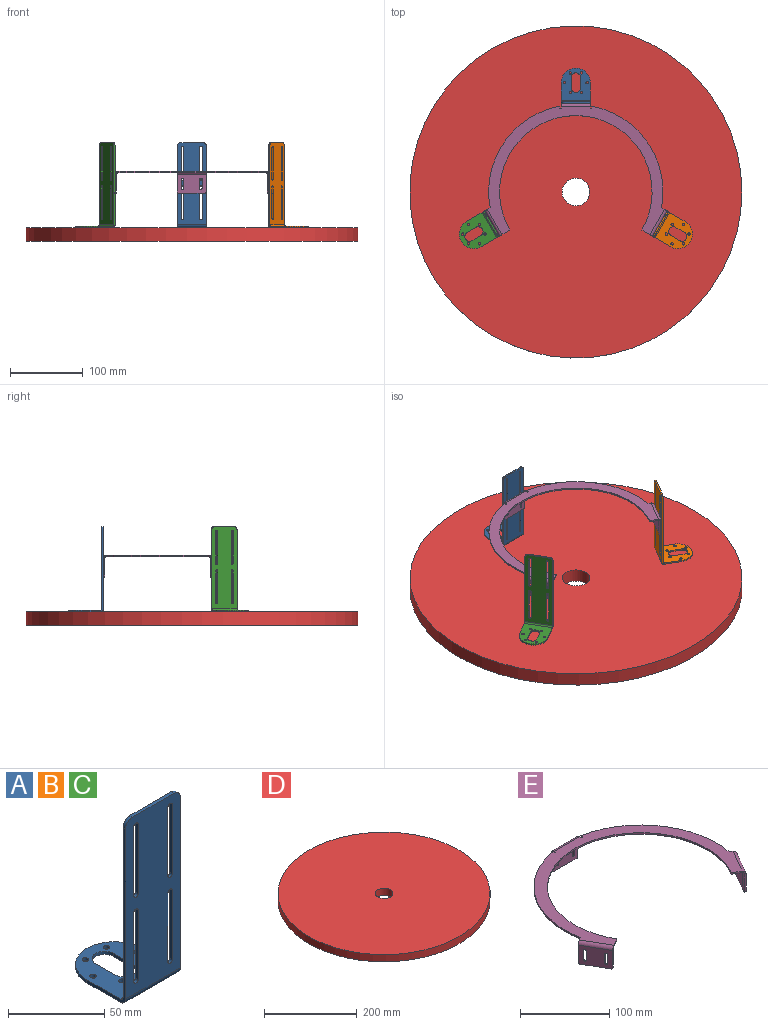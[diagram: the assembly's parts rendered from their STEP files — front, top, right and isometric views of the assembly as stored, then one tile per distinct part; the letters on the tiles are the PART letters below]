
ASSEMBLY  parts=5 mates=6
PART A: 38 faces, bbox 40x48.5x117 mm
  f0: plane 113x40mm, normal (0,1,0), area 3916.5mm2, adj f1,f3,f4,f5,f6,f7,f8,f9
  f1: cylinder r=1.6mm len=3.2mm, axis (0,-1,0), area 10.1mm2, adj f0,f2,f36,f37
  f2: plane 113x40mm, normal (0,-1,0), area 3916.5mm2, adj f1,f3,f4,f5,f6,f7,f8,f9
  f3: plane 43.8x2mm, normal (-1,0,0), area 87.6mm2, adj f0,f2,f5,f6
  f4: plane 43.8x2mm, normal (1,0,0), area 87.6mm2, adj f0,f2,f5,f6
  f5: cylinder r=1.6mm len=3.2mm, axis (0,-1,0), area 10.1mm2, adj f0,f2,f3,f4
  f6: cylinder r=1.6mm len=3.2mm, axis (0,-1,0), area 10.1mm2, adj f0,f2,f3,f4
  f7: cylinder r=1.6mm len=3.2mm, axis (0,-1,0), area 10.1mm2, adj f0,f2,f36,f37
  f8: cylinder r=1.6mm len=3.2mm, axis (0,-1,0), area 10.1mm2, adj f0,f2,f32,f34
  f9: cylinder r=1.6mm len=3.2mm, axis (0,-1,0), area 10.1mm2, adj f0,f2,f32,f34
  f10: cylinder r=1.6mm len=3.2mm, axis (0,-1,0), area 10.1mm2, adj f0,f2,f31,f35
  f11: cylinder r=5mm len=5mm, axis (0,1,0), area 15.7mm2, adj f0,f2,f14,f33
  f12: cylinder r=5mm len=5mm, axis (0,-1,0), area 15.7mm2, adj f0,f2,f15,f33
  f13: cylinder r=1.6mm len=3.2mm, axis (0,-1,0), area 10.1mm2, adj f0,f2,f31,f35
  f14: plane 112x28.5mm, normal (1,0,0), area 274.4mm2, adj f0,f2,f11,f16,f17,f18,f29,f30
  f15: plane 112x28.5mm, normal (-1,0,0), area 274.4mm2, adj f0,f2,f12,f16,f17,f18,f29,f30
  f16: cylinder r=20mm len=40mm, axis (0,0,-1), area 125.7mm2, adj f14,f15,f17,f18
  f17: plane 44.5x40mm, normal (0,0,-1), area 1242.3mm2, adj f14,f15,f16,f19,f20,f21,f22,f23
  f18: plane 44.5x40mm, normal (0,0,1), area 1242.3mm2, adj f14,f15,f16,f19,f20,f21,f22,f23
  f19: cylinder r=1.65mm len=3.3mm, axis (0,0,1), area 20.7mm2, adj f17,f18
  f20: cylinder r=1.65mm len=3.3mm, axis (0,0,1), area 20.7mm2, adj f17,f18
  f21: cylinder r=1.65mm len=3.3mm, axis (0,0,1), area 20.7mm2, adj f17,f18
  f22: cylinder r=1.65mm len=3.3mm, axis (0,0,1), area 20.7mm2, adj f17,f18
  f23: cylinder r=1.65mm len=3.3mm, axis (0,0,1), area 20.7mm2, adj f17,f18
  f24: cylinder r=1.65mm len=3.3mm, axis (0,0,1), area 20.7mm2, adj f17,f18
  f25: plane 14x2mm, normal (-1,0,0), area 28mm2, adj f17,f18,f26,f28
  f26: cylinder r=6.5mm len=13mm, axis (0,0,1), area 40.8mm2, adj f17,f18,f25,f27
  f27: plane 14x2mm, normal (1,0,0), area 28mm2, adj f17,f18,f26,f28
  f28: cylinder r=6.5mm len=13mm, axis (0,0,1), area 40.8mm2, adj f17,f18,f25,f27
  f29: cylinder r=4mm len=40mm, axis (-1,0,0), area 251.3mm2, adj f2,f14,f15,f17
  f30: cylinder r=2mm len=40mm, axis (-1,0,0), area 125.7mm2, adj f0,f14,f15,f18
  f31: plane 43.8x2mm, normal (-1,0,0), area 87.6mm2, adj f0,f2,f10,f13
  f32: plane 43.8x2mm, normal (-1,0,0), area 87.6mm2, adj f0,f2,f8,f9
  f33: plane 30x2mm, normal (0,0,1), area 60mm2, adj f0,f2,f11,f12
  f34: plane 43.8x2mm, normal (1,0,0), area 87.6mm2, adj f0,f2,f8,f9
  f35: plane 43.8x2mm, normal (1,0,0), area 87.6mm2, adj f0,f2,f10,f13
  f36: plane 43.8x2mm, normal (1,0,0), area 87.6mm2, adj f0,f1,f2,f7
  f37: plane 43.8x2mm, normal (-1,0,0), area 87.6mm2, adj f0,f1,f2,f7
PART B: same geometry as A
PART C: same geometry as A
PART D: 4 faces, bbox 457.2x457.2x19.1 mm
  f0: cylinder r=19.05mm len=38.1mm, axis (0,0,-1), area 2280.2mm2, adj f2,f3
  f1: cylinder r=228.6mm len=457.2mm, axis (0,0,-1), area 27362.2mm2, adj f2,f3
  f2: plane 457.2x457.2mm, normal (0,0,1), area 163033.1mm2, adj f0,f1
  f3: plane 457.2x457.2mm, normal (0,0,-1), area 163033.1mm2, adj f0,f1
PART E: 62 faces, bbox 251.3x183x30 mm
  f0: cylinder r=120mm len=139.63mm, axis (0,0,-1), area 374mm2, adj f5,f6,f8,f61
  f1: cylinder r=120mm len=139.63mm, axis (0,0,-1), area 374mm2, adj f5,f6,f7,f12
  f2: cylinder r=1.6mm len=3.77mm, axis (-0.87,0.5,0), area 10.1mm2, adj f42,f43,f45,f46
  f3: cylinder r=1.6mm len=3.77mm, axis (-0.87,0.5,0), area 10.1mm2, adj f42,f43,f47,f48
  f4: cylinder r=1.6mm len=3.77mm, axis (-0.87,0.5,0), area 10.1mm2, adj f42,f43,f47,f48
  f5: plane 243.86x176.55mm, normal (0,0,1), area 6979.9mm2, adj f0,f1,f7,f8,f9,f10,f11,f12
  f6: plane 243.86x176.55mm, normal (0,0,-1), area 6979.9mm2, adj f0,f1,f7,f8,f9,f10,f11,f12
  f7: plane 2x1.26mm, normal (0,1,0), area 2.5mm2, adj f1,f5,f6,f16
  f8: plane 28.4x7.68mm, normal (0.5,0.87,0), area 67.7mm2, adj f0,f5,f6,f35,f40,f41,f42,f43
  f9: plane 28.4x14.72mm, normal (-0.5,-0.87,0), area 84mm2, adj f5,f6,f10,f36,f40,f41,f42,f43
  f10: cylinder r=105mm len=210mm, axis (0,0,-1), area 879.6mm2, adj f5,f6,f9,f11
  f11: plane 28.4x14.72mm, normal (0.5,-0.87,0), area 84mm2, adj f5,f6,f10,f22,f30,f31,f32,f33
  f12: plane 28.4x7.68mm, normal (-0.5,0.87,0), area 67.7mm2, adj f1,f5,f6,f20,f30,f31,f32,f33
  f13: plane 28.4x6.69mm, normal (1,0,0), area 63.3mm2, adj f5,f6,f15,f39,f49,f50,f59,f60
  f14: plane 2.39x2mm, normal (-1,0,0), area 4.8mm2, adj f5,f6,f15,f61
  f15: cylinder r=1.06mm len=2.13mm, axis (0,0,-1), area 6.7mm2, adj f5,f6,f13,f14
  f16: plane 2.39x2mm, normal (1,0,0), area 4.8mm2, adj f5,f6,f7,f18
  f17: plane 28.4x6.69mm, normal (-1,0,0), area 63.3mm2, adj f5,f6,f18,f37,f49,f50,f59,f60
  f18: cylinder r=1.06mm len=2.13mm, axis (0,0,-1), area 6.7mm2, adj f5,f6,f16,f17
  f19: cylinder r=1.6mm len=3.77mm, axis (0.87,0.5,0), area 10.1mm2, adj f25,f26,f30,f31
  f20: cylinder r=1.6mm len=2.53mm, axis (-0.87,-0.5,0), area 5mm2, adj f12,f29,f30,f31
  f21: cylinder r=1.6mm len=3.77mm, axis (0.87,0.5,0), area 10.1mm2, adj f27,f28,f30,f31
  f22: cylinder r=1.6mm len=2.53mm, axis (-0.87,-0.5,0), area 5mm2, adj f11,f29,f30,f31
  f23: cylinder r=1.6mm len=3.77mm, axis (0.87,0.5,0), area 10.1mm2, adj f25,f26,f30,f31
  f24: cylinder r=1.6mm len=3.77mm, axis (0.87,0.5,0), area 10.1mm2, adj f27,f28,f30,f31
  f25: plane 12.5x1.73mm, normal (0.5,-0.87,0), area 25mm2, adj f19,f23,f30,f31
  f26: plane 12.5x1.73mm, normal (-0.5,0.87,0), area 25mm2, adj f19,f23,f30,f31
  f27: plane 12.5x1.73mm, normal (0.5,-0.87,0), area 25mm2, adj f21,f24,f30,f31
  f28: plane 12.5x1.73mm, normal (-0.5,0.87,0), area 25mm2, adj f21,f24,f30,f31
  f29: plane 32.87x20.13mm, normal (0,0,-1), area 73.6mm2, adj f20,f22,f30,f31
  f30: plane 34.64x25.7mm, normal (-0.87,-0.5,0), area 930.8mm2, adj f11,f12,f19,f20,f21,f22,f23,f24
  f31: plane 34.64x25.7mm, normal (0.87,0.5,0), area 930.8mm2, adj f11,f12,f19,f20,f21,f22,f23,f24
  f32: cylinder r=2.3mm len=35.79mm, axis (-0.5,0.87,0), area 144.5mm2, adj f6,f11,f12,f31
  f33: cylinder r=4.3mm len=36.79mm, axis (-0.5,0.87,0), area 270.2mm2, adj f5,f11,f12,f30
  f34: cylinder r=1.6mm len=3.77mm, axis (-0.87,0.5,0), area 10.1mm2, adj f42,f43,f45,f46
  f35: cylinder r=1.6mm len=2.53mm, axis (0.87,-0.5,0), area 5mm2, adj f8,f42,f43,f44
  f36: cylinder r=1.6mm len=2.53mm, axis (0.87,-0.5,0), area 5mm2, adj f9,f42,f43,f44
  f37: cylinder r=1.6mm len=2mm, axis (0,1,0), area 5mm2, adj f17,f49,f50,f58
  f38: cylinder r=1.6mm len=3.2mm, axis (0,-1,0), area 10.1mm2, adj f49,f50,f54,f55
  f39: cylinder r=1.6mm len=2mm, axis (0,1,0), area 5mm2, adj f13,f49,f50,f58
  f40: cylinder r=4.3mm len=36.79mm, axis (-0.5,-0.87,0), area 270.2mm2, adj f5,f8,f9,f43
  f41: cylinder r=2.3mm len=35.79mm, axis (-0.5,-0.87,0), area 144.5mm2, adj f6,f8,f9,f42
  f42: plane 34.64x25.7mm, normal (-0.87,0.5,0), area 930.8mm2, adj f2,f3,f4,f8,f9,f34,f35,f36
  f43: plane 34.64x25.7mm, normal (0.87,-0.5,0), area 930.8mm2, adj f2,f3,f4,f8,f9,f34,f35,f36
  f44: plane 32.87x20.13mm, normal (0,0,-1), area 73.6mm2, adj f35,f36,f42,f43
  f45: plane 12.5x1.73mm, normal (0.5,0.87,0), area 25mm2, adj f2,f34,f42,f43
  f46: plane 12.5x1.73mm, normal (-0.5,-0.87,0), area 25mm2, adj f2,f34,f42,f43
  f47: plane 12.5x1.73mm, normal (-0.5,-0.87,0), area 25mm2, adj f3,f4,f42,f43
  f48: plane 12.5x1.73mm, normal (0.5,0.87,0), area 25mm2, adj f3,f4,f42,f43
  f49: plane 40x25.7mm, normal (0,-1,0), area 930.8mm2, adj f13,f17,f37,f38,f39,f51,f52,f53
  f50: plane 40x25.7mm, normal (0,1,0), area 930.8mm2, adj f13,f17,f37,f38,f39,f51,f52,f53
  f51: cylinder r=1.6mm len=3.2mm, axis (0,-1,0), area 10.1mm2, adj f49,f50,f54,f55
  f52: cylinder r=1.6mm len=3.2mm, axis (0,-1,0), area 10.1mm2, adj f49,f50,f56,f57
  f53: cylinder r=1.6mm len=3.2mm, axis (0,-1,0), area 10.1mm2, adj f49,f50,f56,f57
  f54: plane 12.5x2mm, normal (-1,0,0), area 25mm2, adj f38,f49,f50,f51
  f55: plane 12.5x2mm, normal (1,0,0), area 25mm2, adj f38,f49,f50,f51
  f56: plane 12.5x2mm, normal (-1,0,0), area 25mm2, adj f49,f50,f52,f53
  f57: plane 12.5x2mm, normal (1,0,0), area 25mm2, adj f49,f50,f52,f53
  f58: plane 36.8x2mm, normal (0,0,-1), area 73.6mm2, adj f37,f39,f49,f50
  f59: cylinder r=2.3mm len=40mm, axis (1,0,0), area 144.5mm2, adj f6,f13,f17,f49
  f60: cylinder r=4.3mm len=40mm, axis (1,0,0), area 270.2mm2, adj f5,f13,f17,f50
  f61: plane 2x1.26mm, normal (0,1,0), area 2.5mm2, adj f0,f5,f6,f14
PLACE A t=(-20,124,2)mm
PLACE B rot(axis=(0,0,-1),120deg) t=(127.39,-27.36,2)mm
PLACE C rot(axis=(0,0,1),120deg) t=(-107.39,-62,2)mm
PLACE D t=(-520.73,0,-19.05)mm
PLACE E t=(0,0,77.37)mm
MATE slider E.f10 <-> D.f1  axis (0,0,-1) through (0,0,76.37)mm
MATE planar D.f1 <-> C.f17  axis (0,0,1) through (0,0,0)mm
MATE fastened B.f2 <-> E.f43  axis (-0.87,0.5,0) through (115.66,-43.68,60.23)mm
MATE parallel C.f20 <-> B.f17  axis (0,0,-1) through (-132.59,-44.51,0)mm
MATE fastened E.f50 <-> A.f2  axis (0,1,0) through (0,122,60.23)mm
MATE fastened E.f30 <-> C.f2  axis (-0.87,-0.5,0) through (-115.66,-43.68,60.23)mm
